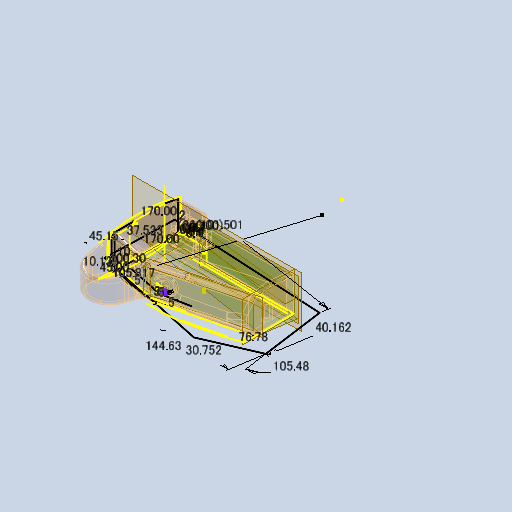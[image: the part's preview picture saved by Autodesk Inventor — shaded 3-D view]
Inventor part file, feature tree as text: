
AUTODESK INVENTOR PART (.ipt)
format: ipt  version: 2025 (Build 290162000, 162)  size: 3,770,368 bytes
history: native  units: in
note: dims shown in document units (in); Inventor stores cm internally (conversion verified against a paired STEP export)
features: extrude x46, sketch x37, fillet x33, other x28, reference x27, chamfer x10, projected_geometry x7, mirror x3
ambient origin geometry x8: Origin, YZ Plane, XZ Plane, XY Plane, X Axis, Y Axis, Z Axis, Center Point
bodies: Body1 (feature_tree)
feature tree (191):
  other  "ソリッド1"
  sketch  "スケッチ1"
  extrude  "押し出し1"  Depth=3.3465in
  sketch  "スケッチ4"
  extrude  "押し出し4"  Depth=0.2756in
  extrude  "押し出し5"  Depth=9.8425in
  extrude  "押し出し6"  Depth=0.8661in TaperAngle=0.0deg
  extrude  "押し出し7"  Depth=0.8268in
  chamfer  "面取り1"  Distance=0.1181in
  chamfer  "面取り2"  Distance=0.1181in
  chamfer  "面取り3"  Distance=1.8504in
  chamfer  "面取り4"  Distance=1.1024in
  other  "作業平面3"
  other  "作業平面5"
  extrude  "押し出し8"  Depth=1.5354in
  other  "作業平面6"
  mirror  "ミラー1"
  chamfer  "面取り5"  Distance=3.3465in
  extrude  "押し出し9"  Depth=3.3465in TaperAngle=0.0deg
  fillet  "フィレット27"  Radius=3.3465in
  fillet  "フィレット28"  Radius=3.3465in
  fillet  "フィレット29"  Radius=0.1181in
  fillet  "フィレット30"  Radius=0.1181in
  fillet  "フィレット32"  Radius=0.1181in
  fillet  "フィレット35"  Radius=0.1181in
  fillet  "フィレット36"  Radius=0.3937in
  fillet  "フィレット37"  Radius=0.1575in
  fillet  "フィレット38"  Radius=0.7087in
  fillet  "フィレット42"  [1 undecoded]
  fillet  "フィレット43"  Radius=0.3543in
  fillet  "フィレット44"  Radius=1.9685in
  fillet  "フィレット45"  Radius=2.0866in
  other  "作業平面7"
  extrude  "押し出し10"  Depth=0.1969in
  fillet  "フィレット46"  Radius=0.1969in
  other  "作業平面8"
  extrude  "押し出し11"  Depth=0.7874in
  sketch  "スケッチ10"
  extrude  "押し出し12"  Depth=0.0787in
  extrude  "押し出し13"  Depth=0.3937in
  chamfer  "面取り6"  Distance=0.1181in
  sketch  "スケッチ11"
  chamfer  "面取り7"  Distance=0.1181in
  extrude  "押し出し14"  Depth=0.0354in
  chamfer  "面取り8"  Distance=0.0394in
  chamfer  "面取り9"  Distance=0.0787in
  extrude  "押し出し15"  Depth=0.0118in
  chamfer  "面取り10"  Distance=0.0354in
  other  "作業平面9"
  other  "作業平面10"
  extrude  "押し出し16"  [1 undecoded]
  fillet  "フィレット47"  Radius=0.0394in
  fillet  "フィレット48"  Radius=0.0394in
  fillet  "フィレット49"  Radius=0.0394in
  mirror  "ミラー7"
  mirror  "ミラー8"
  fillet  "フィレット58"  Radius=0.8268in
  fillet  "フィレット59"  Radius=0.0787in
  fillet  "フィレット60"  Radius=0.8268in
  fillet  "フィレット61"  Radius=1.1681in
  fillet  "フィレット62"  Radius=1.1681in
  fillet  "フィレット63"  Radius=0.6299in
  other  "作業平面11"
  extrude  "押し出し17"  TaperAngle=45.0deg  [1 undecoded]
  extrude  "押し出し18"  Depth=0.3937in
  extrude  "押し出し19"  Depth=1.1811in TaperAngle=0.0deg
  extrude  "押し出し20"  Depth=0.3543in TaperAngle=45.0deg
  other  "作業平面13"
  extrude  "押し出し21"  Depth=0.0787in
  fillet  "フィレット66"  Radius=0.1181in
  fillet  "フィレット67"  Radius=0.0709in
  extrude  "押し出し22"  Depth=0.0394in TaperAngle=45.0deg
  other  "作業平面14"
  extrude  "押し出し23"  Depth=0.0394in TaperAngle=45.0deg
  other  "作業平面15"
  extrude  "押し出し24"  Depth=0.0591in TaperAngle=0.0deg
  extrude  "押し出し25"  Depth=0.1969in TaperAngle=45.0deg
  other  "作業平面16"
  extrude  "押し出し26"  Depth=0.0591in TaperAngle=0.0deg
  extrude  "押し出し27"  Depth=3.937in
  other  "作業平面17"
  extrude  "押し出し28"  Depth=1.9685in
  extrude  "押し出し29"  Depth=0.1181in
  sketch  "スケッチ29"
  extrude  "押し出し30"  Depth=0.1181in
  extrude  "押し出し31"  Depth=0.0787in
  extrude  "押し出し32"  Depth=0.0197in
  extrude  "押し出し33"  Depth=0.0197in
  other  "作業平面18"
  extrude  "押し出し34"  Depth=0.3937in
  extrude  "押し出し35"  Depth=0.1181in
  fillet  "フィレット68"  [1 undecoded]
  fillet  "フィレット69"  Radius=1.1811in
  fillet  "フィレット70"  Radius=0.0787in
  fillet  "フィレット71"  Radius=0.1181in
  fillet  "フィレット72"  Radius=0.0197in
  extrude  "押し出し36"  Depth=0.0787in TaperAngle=0.0deg
  other  "作業平面19"
  fillet  "フィレット74"  Radius=0.9949in
  fillet  "フィレット75"  Radius=0.3937in
  fillet  "フィレット76"  Radius=0.0472in
  sketch  "スケッチ33"
  extrude  "押し出し39"  Depth=0.0669in
  extrude  "押し出し40"  Depth=0.0079in
  other  "作業平面21"
  extrude  "押し出し41"  Depth=0.2362in
  extrude  "押し出し42"  Depth=0.3543in
  sketch  "スケッチ37"
  extrude  "押し出し43"  Depth=0.3543in
  other  "作業平面22"
  extrude  "押し出し44"  Depth=0.2362in
  sketch  "スケッチ39"
  extrude  "押し出し45"  Depth=0.0079in
  extrude  "押し出し46"  Depth=0.0787in
  extrude  "押し出し47"  Depth=0.0079in
  extrude  "押し出し48"  Depth=0.1181in
  extrude  "押し出し49"  Depth=0.0787in
  extrude  "押し出し50"  Depth=0.0079in
  projected_geometry  "投影ループ2"
  sketch  "スケッチ5"
  projected_geometry  "投影ループ3"
  sketch  "スケッチ6"
  projected_geometry  "投影ループ4"
  other  "作業平面2"
  other  "作業平面4"
  sketch  "スケッチ7"
  sketch  "スケッチ8"
  projected_geometry  "投影ループ5"
  sketch  "スケッチ9"
  sketch  "スケッチ12"
  sketch  "スケッチ13"
  sketch  "スケッチ14"
  sketch  "スケッチ15"
  sketch  "スケッチ16"
  sketch  "スケッチ18"
  sketch  "スケッチ19"
  sketch  "スケッチ20"
  sketch  "スケッチ21"
  reference  "参照1"
  reference  "参照2"
  reference  "参照3"
  reference  "参照4"
  reference  "参照5"
  sketch  "スケッチ22"
  reference  "参照6"
  reference  "参照7"
  sketch  "スケッチ23"
  reference  "参照8"
  reference  "参照9"
  reference  "参照10"
  reference  "参照11"
  reference  "参照12"
  reference  "参照13"
  sketch  "スケッチ24"
  projected_geometry  "投影ループ6"
  sketch  "スケッチ25"
  sketch  "スケッチ26"
  sketch  "スケッチ27"
  sketch  "スケッチ28"
  reference  "参照14"
  reference  "参照15"
  other  "スケッチ円形状パターン1"
  sketch  "スケッチ30"
  reference  "参照16"
  sketch  "スケッチ31"
  reference  "参照17"
  reference  "参照18"
  reference  "参照19"
  reference  "参照21"
  reference  "参照22"
  reference  "参照23"
  reference  "参照24"
  reference  "参照25"
  reference  "参照29"
  sketch  "スケッチ32"
  sketch  "スケッチ35"
  sketch  "スケッチ36"
  sketch  "スケッチ38"
  reference  "参照30"
  projected_geometry  "投影ループ7"
  projected_geometry  "投影ループ8"
  sketch  "スケッチ40"
  reference  "参照31"
  sketch  "スケッチ41"
  other  "<userpath>\OneDrive\ドキュメント\New Controller\Hardware\Assembly.iam"
  other  "Assembly.iam"
  other  "Nano33BLE:1"
  other  "Cuicuit:1"
  other  "switch:1"
  other  "mini vibrator:1"
  other  "Body_compleat02:1"
note: 4 required parameter values undecoded (feature->parameter linkage not recoverable at this tier; creation-order binding heuristic only, values carry confidence <= 0.55)
